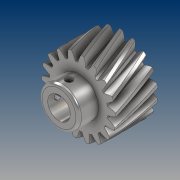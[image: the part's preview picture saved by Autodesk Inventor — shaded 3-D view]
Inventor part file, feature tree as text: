
AUTODESK INVENTOR PART (.ipt)
format: ipt  version: 2021 (Build 250183000, 183)  size: 557,568 bytes
history: native  units: mm (DEFAULTED — no unit token found)
features: extrude x4, sketch x4, plane x3, other x3, projected_geometry x2, pattern_circular x1, fillet x1
ambient origin geometry x8: Origin, YZ Plane, XZ Plane, XY Plane, X Axis, Y Axis, Z Axis, Center Point
bodies: Solid1 (feature_tree)
feature tree (18):
  extrude  "Extrusion1"  Depth=15.0mm TaperAngle=0.0deg
  plane  "Work Plane2"
  plane  "Work Plane8"
  plane  "Work Plane9"
  other  "Spur Gear"
  sketch  "Sketch3"  dims[d16=59.86mm d17=0.0mm d34=1.745329mm]
  extrude  "Extrusion2"  Depth=10.0mm TaperAngle=0.0deg
  extrude  "Extrusion3"  Depth=1.745329mm TaperAngle=0.0deg
  extrude  "Extrusion4"  TaperAngle=0.0deg  [1 undecoded]
  pattern_circular  "Circular Pattern1"  [2 undecoded]
  fillet  "Fillet1"  Radius=59.86mm
  sketch  "Sketch1"  dims[d0=26.444mm d1=15.0mm d2=0.0mm]
  sketch  "Sketch2"  dims[d3=23.944mm d4=10.0mm d5=0.0mm]
  other  "Srf1"
  projected_geometry  "Projected Loop1"
  sketch  "Sketch4"  dims[d39=0.0mm d41=0.0mm d43=59.86mm d46=59.86mm d47=0.0mm d48=0.0mm d49=8.0mm d50=3.0mm d51=15.75mm d52=0.0mm d53=7.0mm d54=0.0mm d55=2.5mm d56=7.0mm d57=0.0mm d58=20.0mm d59=90.0deg d61=1.0mm]
  projected_geometry  "Projected Loop2"
  other  "Pitch Diameter"
note: 3 required parameter values undecoded (feature->parameter linkage not recoverable at this tier; creation-order binding heuristic only, values carry confidence <= 0.55)
